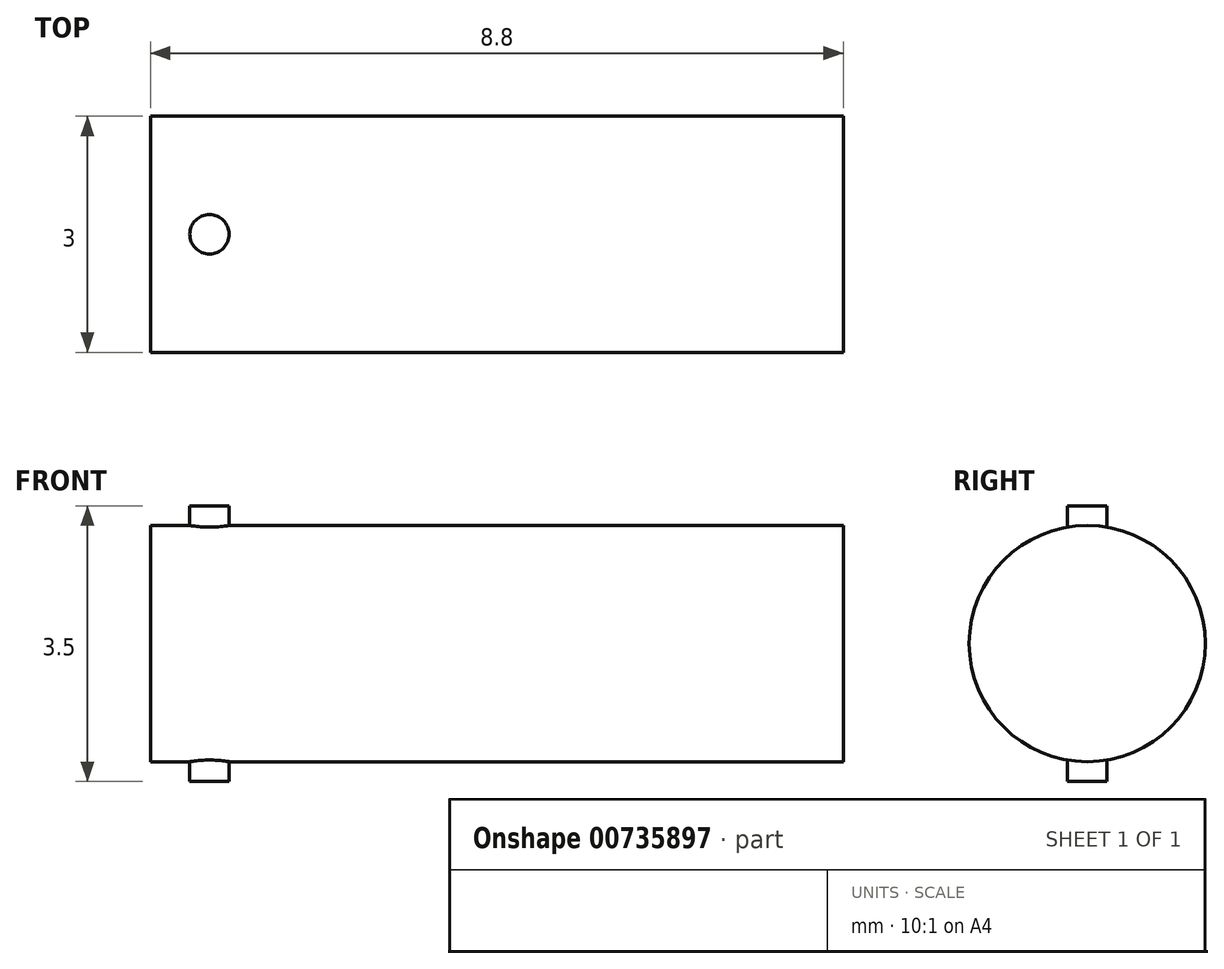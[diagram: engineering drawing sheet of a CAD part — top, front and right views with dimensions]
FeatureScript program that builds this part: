
annotation { "Feature Type Name" : "Feature", "Feature Type Description" : "" }
export const myFeature = defineFeature(function(context is Context, id is Id, definition is map)
    precondition{}
    {
        {
            var Q0;
            Q0=qCreatedBy(makeId("Right.planeOp"),FACE);
            var sketch = newSketch(context, id + "F0", { "sketchPlane" : qUnion([Q0])});
            skArc(sketch, "E0", {"start": v(1.5, 0) * mm, "mid": v(0, 1.5) * mm, "end": v(-1.5, 0) * mm});
            skLineSegment(sketch, "E1", {"start": v(-1.5, 0) * mm, "end": v(1.5, 0) * mm});
            skSolve(sketch);
        }
        {
            var Q0;
            Q0=makeQuery(id+"F0.imprint","IMPRINT",FACE,{"disambiguationData":[TD([[makeQuery(id+"F0.imprint","IMPRINT",EDGE,{"derivedFrom":sQuery(id+"F0.wireOp",EDGE,"E0")}),1.0]])]});
            extrude(context, id + "F1", {"entities" : qUnion([Q0]), "depth" : 8.8 * mm, "offsetDistance" : 25 * mm});
        }
        {
            var Q0;
            Q0=makeQuery(id+"F1.opExtrude","SWEPT_FACE",FACE,{"disambiguationData":[OSD([sQuery(id+"F0.wireOp",EDGE,"E1")])]});
            var sketch = newSketch(context, id + "F2", { "sketchPlane" : qUnion([Q0])});
            skCircle(sketch, "E2", {"center": v(0.75, 0) * mm, "radius": 0.25 * mm});
            skSolve(sketch);
        }
        {
            var Q0;
            Q0=makeQuery(id+"F2.imprint","IMPRINT",FACE,{"disambiguationData":[TD([[makeQuery(id+"F2.imprint","IMPRINT",EDGE,{"derivedFrom":sQuery(id+"F2.wireOp",EDGE,"E2")}),1.0]])]});
            extrude(context, id + "F3", {"entities" : qUnion([Q0]), "operationType" : NewBodyOperationType.ADD, "endBound" : BoundingType.SYMMETRIC, "depth" : 3.5 * mm, "offsetDistance" : 25 * mm});
        }
        {
            var Q0;
            Q0=makeQuery(id+"F1.opExtrude","SWEPT_BODY",BODY,{"disambiguationData":[OSD([sQuery(id+"F0.wireOp",EDGE,"E0"),sQuery(id+"F0.wireOp",EDGE,"E1")])]});
            var Q1;
            Q1=qCreatedBy(makeId("Top.planeOp"),FACE);
            mirror(context, id + "F4", {"operationType" : NewBodyOperationType.ADD, "entities" : qUnion([Q0]), "mirrorPlane" : qUnion([Q1])});
        }
    });
